# Revit family: Montagedeckel - OKA D 500 R9-AA
name_source: partatom
category: Generic Models
revit_build: Autodesk Revit 2017 (Build: 20160225_1515(x64)
units: mm (PartAtom-declared; Revit-internal decimal feet)

## family parameters
Always vertical = Yes
Can host rebar = No
Cut with Voids When Loaded = No
Part Type = Normal
Room Calculation Point = No
Round Connector Dimension = Use Diameter
Shared = No
Work Plane-Based = No

## types (1)
- OKA D 500 R9
    Article Type = OKA D 500 R9
    GTIN = 4012195245483
    Height = 4 mm  [stored 0.0131234 ft]
    Length = 500 mm  [stored 1.64042 ft]
    Manufacturer = Obo-Bettermann
    Manufacturer Art.No. = 7425122
    Material = Strip-galvanised
    URL = http://www.obo-bettermann.com
    Width = 400 mm  [stored 1.31234 ft]

note: [stored X ft] marks values corroborated as IEEE doubles in the binary element streams (Revit-internal decimal feet)

## geometry (parser evidence)
native form markers: Sweep x2
no freeform markers — native parametric forms only
